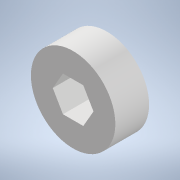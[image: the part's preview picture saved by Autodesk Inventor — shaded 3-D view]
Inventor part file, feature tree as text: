
AUTODESK INVENTOR PART (.ipt)
format: ipt  version: 2022 (Build 260153000, 153)  size: 122,880 bytes
history: native  units: mm
features: reference x7, other x4, extrude x2, sketch x1
ambient origin geometry x8: Origin, YZ Plane, XZ Plane, XY Plane, X Axis, Y Axis, Z Axis, Center Point
bodies: Solid1 (feature_tree)
feature tree (14):
  extrude  "Extrusion1"  Depth=10.0mm
  extrude  "Extrusion2"  Depth=10.0mm TaperAngle=360.0deg
  reference  "Reference1"
  reference  "Reference2"
  reference  "Reference3"
  reference  "Reference4"
  reference  "Reference5"
  reference  "Reference6"
  sketch  "Sketch2"  dims[d1=6.0mm d2=0.0mm d4=3.1mm d5=60.0mm d7=360.0deg d9=0.45mm d10=10.0mm d11=0.0mm]
  reference  "Reference7"
  other  "Caja_Reductora.iam"
  other  "Hombro_Ejes:6"
  other  "Caja_Reductora_.iam"
  other  "Rodamiento_Ejes:6"
